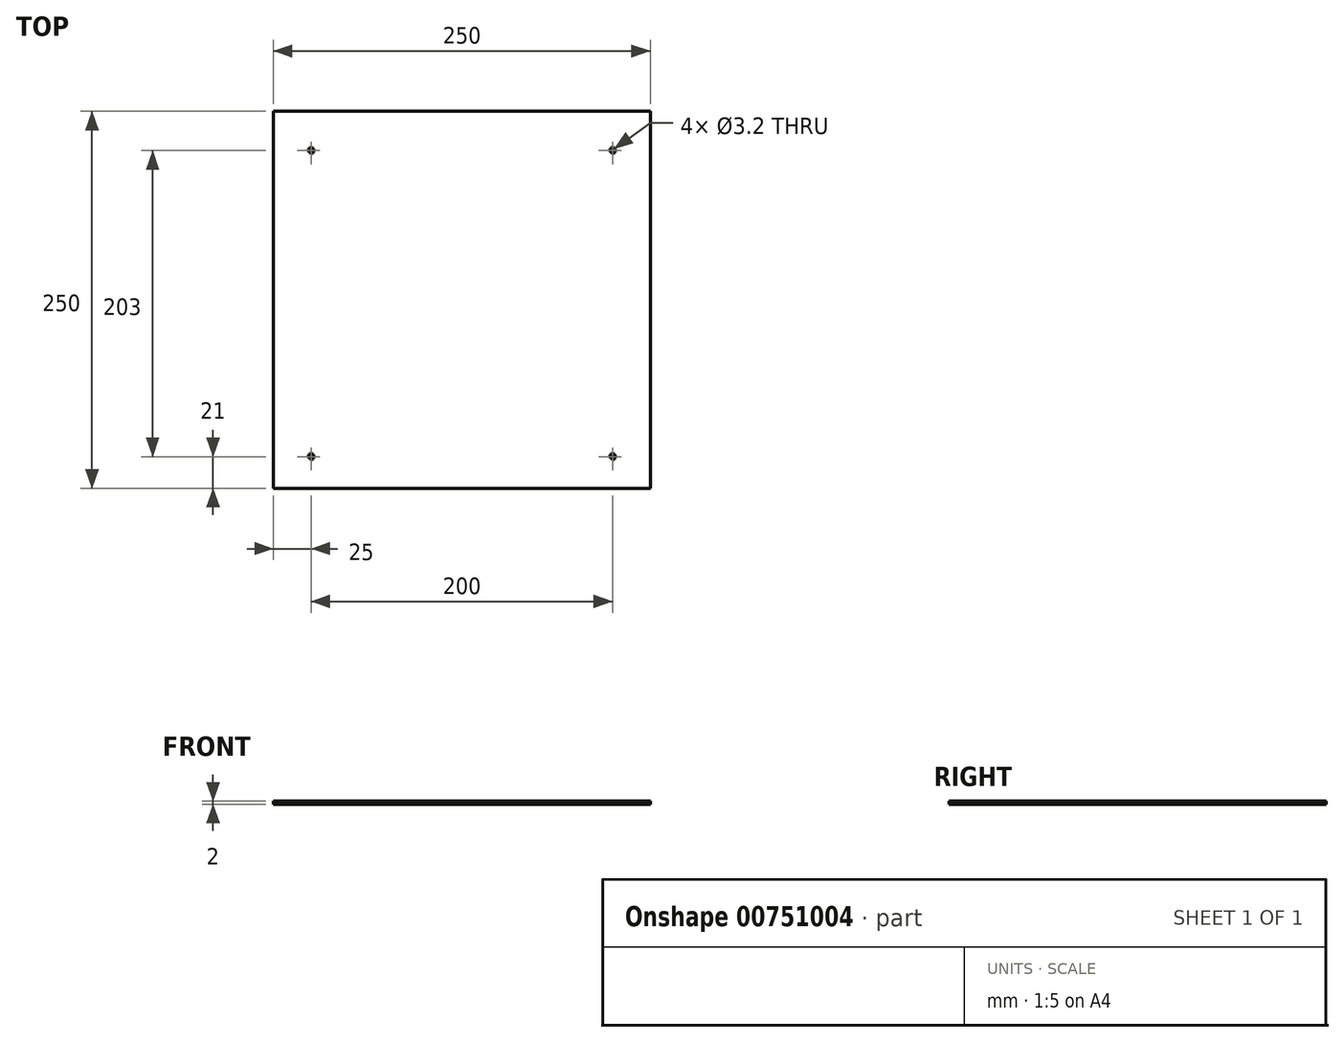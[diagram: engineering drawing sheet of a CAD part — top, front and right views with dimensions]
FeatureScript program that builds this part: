
annotation { "Feature Type Name" : "Feature", "Feature Type Description" : "" }
export const myFeature = defineFeature(function(context is Context, id is Id, definition is map)
    precondition{}
    {
        {
            var Q0;
            Q0=qCreatedBy(makeId("Top.planeOp"),FACE);
            var sketch = newSketch(context, id + "F0", { "sketchPlane" : qUnion([Q0])});
            skLineSegment(sketch, "E0.bottom", {"start": v(125, -125) * mm, "end": v(-125, -125) * mm});
            skLineSegment(sketch, "E0.top", {"start": v(125, 125) * mm, "end": v(-125, 125) * mm});
            skLineSegment(sketch, "E0.left", {"start": v(125, -125) * mm, "end": v(125, 125) * mm});
            skLineSegment(sketch, "E0.right", {"start": v(-125, -125) * mm, "end": v(-125, 125) * mm});
            skPoint(sketch, "E0.middle", {"position": v(0, 0) * mm});
            skLineSegment(sketch, "E1", {"start": v(100, -125) * mm, "end": v(100, -104) * mm, "construction": true});
            skLineSegment(sketch, "E2", {"start": v(100, -104) * mm, "end": v(125, -104) * mm, "construction": true});
            skLineSegment(sketch, "E3", {"start": v(100, 125) * mm, "end": v(100, 99) * mm, "construction": true});
            skLineSegment(sketch, "E4", {"start": v(100, 99) * mm, "end": v(125, 99) * mm, "construction": true});
            skLineSegment(sketch, "E5", {"start": v(-100, 125) * mm, "end": v(-100, 99) * mm, "construction": true});
            skLineSegment(sketch, "E6", {"start": v(-100, 99) * mm, "end": v(-125, 99) * mm, "construction": true});
            skLineSegment(sketch, "E7", {"start": v(-125, -104) * mm, "end": v(-100, -104) * mm});
            skLineSegment(sketch, "E8", {"start": v(-100, -104) * mm, "end": v(-100, -125) * mm});
            skSolve(sketch);
        }
        {
            var Q0;
            Q0=makeQuery(id+"F0.imprint","IMPRINT",FACE,{"disambiguationData":[TD([[makeQuery(id+"F0.imprint","IMPRINT",EDGE,{"derivedFrom":sQuery(id+"F0.wireOp",EDGE,"E0.bottom")}),-1.0]])]});
            var Q1;
            {var subQ1=sQuery(id+"F0.wireOp",EDGE,"E0.top");Q1=makeQuery(id+"F0.imprint","IMPRINT",FACE,{"disambiguationData":[TD([[makeQuery(id+"F0.imprint","IMPRINT",EDGE,{"derivedFrom":subQ1}),1.0]])]});}
            extrude(context, id + "F1", {"entities" : qUnion([Q0, Q1]), "depth" : 2 * mm, "offsetDistance" : 25 * mm});
        }
        {
            var Q0;
            Q0=sQuery(id+"F0.wireOp",VERTEX,"E5.end");
            var Q1;
            Q1=sQuery(id+"F0.wireOp",VERTEX,"E3.end");
            var Q2;
            Q2=sQuery(id+"F0.wireOp",VERTEX,"E1.end");
            var Q3;
            Q3=sQuery(id+"F0.wireOp",VERTEX,"E7.end");
            var Q4;
            Q4=makeQuery(id+"F1.opExtrude","SWEPT_BODY",BODY,{"disambiguationData":[OSD([sQuery(id+"F0.wireOp",EDGE,"E0.bottom"),sQuery(id+"F0.wireOp",EDGE,"E0.top"),sQuery(id+"F0.wireOp",EDGE,"E0.left"),sQuery(id+"F0.wireOp",EDGE,"E0.right")])]});
            hole(context, id + "F2", {"style" : HoleStyle.C_SINK, "endStyle" : HoleEndStyle.THROUGH, "oppositeDirection" : true, "holeDiameter" : 3.2 * mm, "cSinkDiameter" : 5 * mm, "cSinkAngle" : 82 * degree, "majorDiameter" : 5 * mm, "isTappedThrough" : true, "tappedDepth" : 12 * mm, "tapClearance" : 3, "locations" : qUnion([Q0, Q1, Q2, Q3]), "scope" : qUnion([Q4])});
        }
    });
